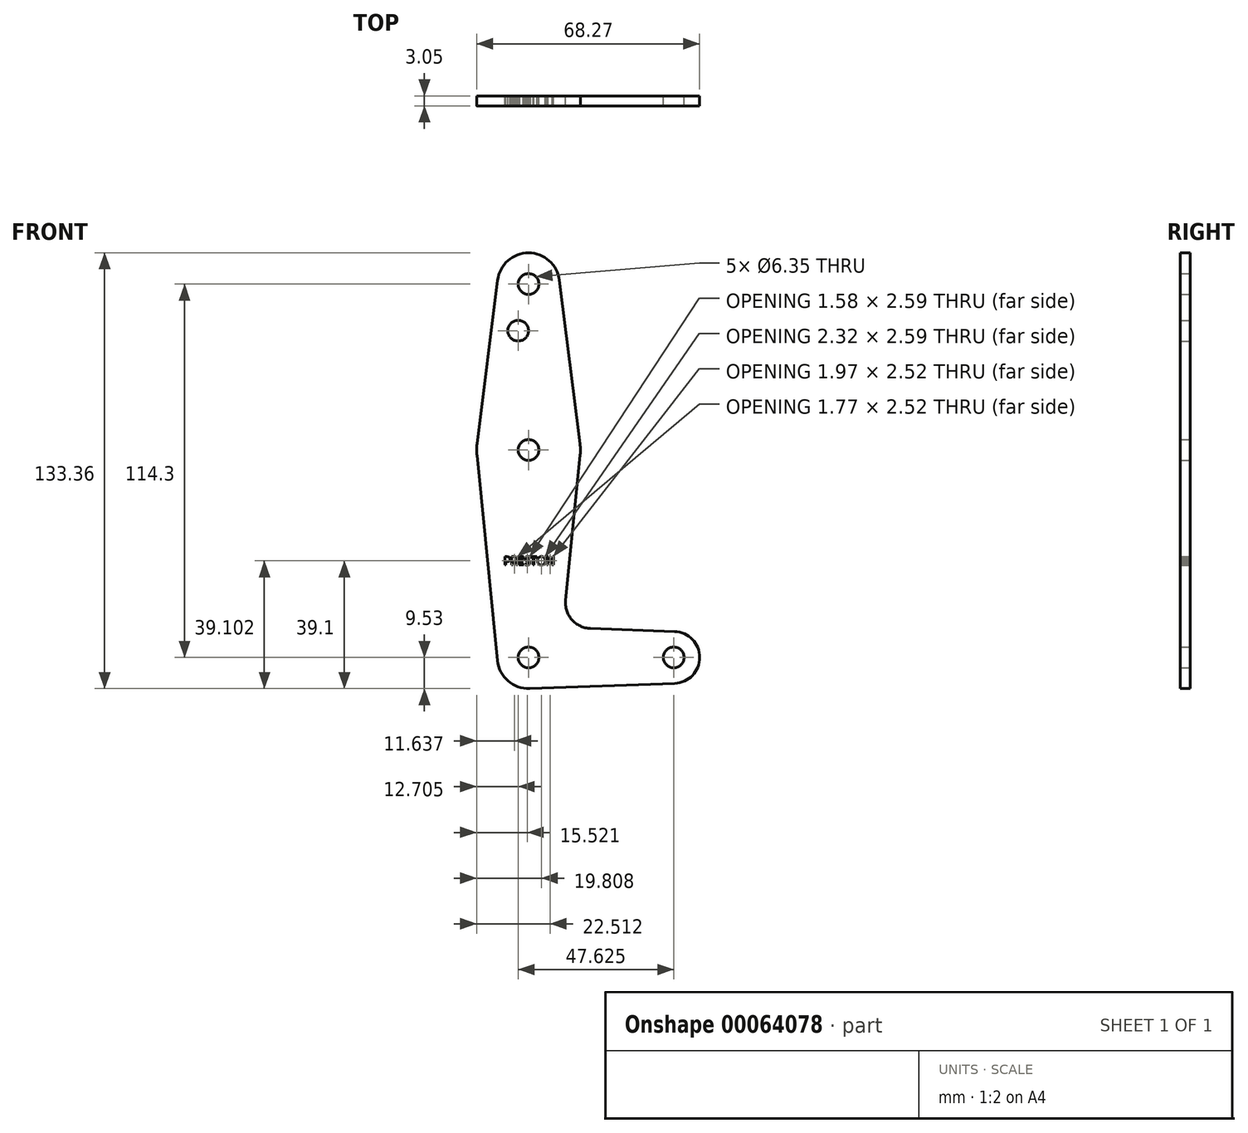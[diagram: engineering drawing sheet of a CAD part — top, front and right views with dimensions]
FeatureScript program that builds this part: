
annotation { "Feature Type Name" : "Feature", "Feature Type Description" : "" }
export const myFeature = defineFeature(function(context is Context, id is Id, definition is map)
    precondition{}
    {
        {
            var Q0;
            Q0=qCreatedBy(makeId("Front.planeOp"),FACE);
            var sketch = newSketch(context, id + "F0", { "sketchPlane" : qUnion([Q0])});
            skLineSegment(sketch, "E0", {"start": v(0, 114.3) * mm, "end": v(0, 0) * mm, "construction": true});
            skLineSegment(sketch, "E1", {"start": v(0, 0) * mm, "end": v(44.45, 0) * mm, "construction": true});
            skCircle(sketch, "E2", {"center": v(0, 114.3) * mm, "radius": 9.53 * mm});
            skCircle(sketch, "E3", {"center": v(0, 63.5) * mm, "radius": 15.88 * mm});
            skCircle(sketch, "E4", {"center": v(0, 0) * mm, "radius": 9.53 * mm});
            skCircle(sketch, "E5", {"center": v(44.45, 0) * mm, "radius": 7.94 * mm});
            skCircle(sketch, "E6", {"center": v(0, 114.3) * mm, "radius": 3.18 * mm});
            skCircle(sketch, "E7", {"center": v(0, 63.5) * mm, "radius": 3.18 * mm});
            skCircle(sketch, "E8", {"center": v(0, 0) * mm, "radius": 3.18 * mm});
            skCircle(sketch, "E9", {"center": v(44.45, 0) * mm, "radius": 3.18 * mm});
            skCircle(sketch, "E10", {"center": v(-3.18, 100.03) * mm, "radius": 3.18 * mm});
            skLineSegment(sketch, "E11", {"start": v(-9.45, 115.5) * mm, "end": v(-15.75, 65.48) * mm});
            skLineSegment(sketch, "E12", {"start": v(9.45, 115.5) * mm, "end": v(15.75, 65.48) * mm});
            skLineSegment(sketch, "E13", {"start": v(-15.8, 61.91) * mm, "end": v(-9.48, -0.95) * mm});
            skLineSegment(sketch, "E14", {"start": v(15.8, 61.91) * mm, "end": v(11.34, 17.6) * mm});
            skLineSegment(sketch, "E15", {"start": v(0.34, -9.52) * mm, "end": v(44.73, -7.93) * mm});
            skLineSegment(sketch, "E16", {"start": v(18.97, 8.85) * mm, "end": v(44.73, 7.93) * mm});
            skArc(sketch, "E17.filletArc", {"start": v(11.34, 17.6) * mm, "mid": v(13.26, 11.57) * mm, "end": v(18.97, 8.85) * mm});
            skText(sketch, "E18", { "text": "PRESTON", "fontName": "OpenSans-Regular.ttf"});
            const initialGuessF0  = {"E18": [-0.0076, 0.02831, 1, 0, 0.00254]};
            skSetInitialGuess(sketch, initialGuessF0);
            skSolve(sketch);
        }
        {
            var Q0;
            Q0 = qSketchRegion(id + "F0", true);
            extrude(context, id + "F1", {"entities" : qUnion([Q0]), "depth" : 3.05 * mm});
        }
    });
